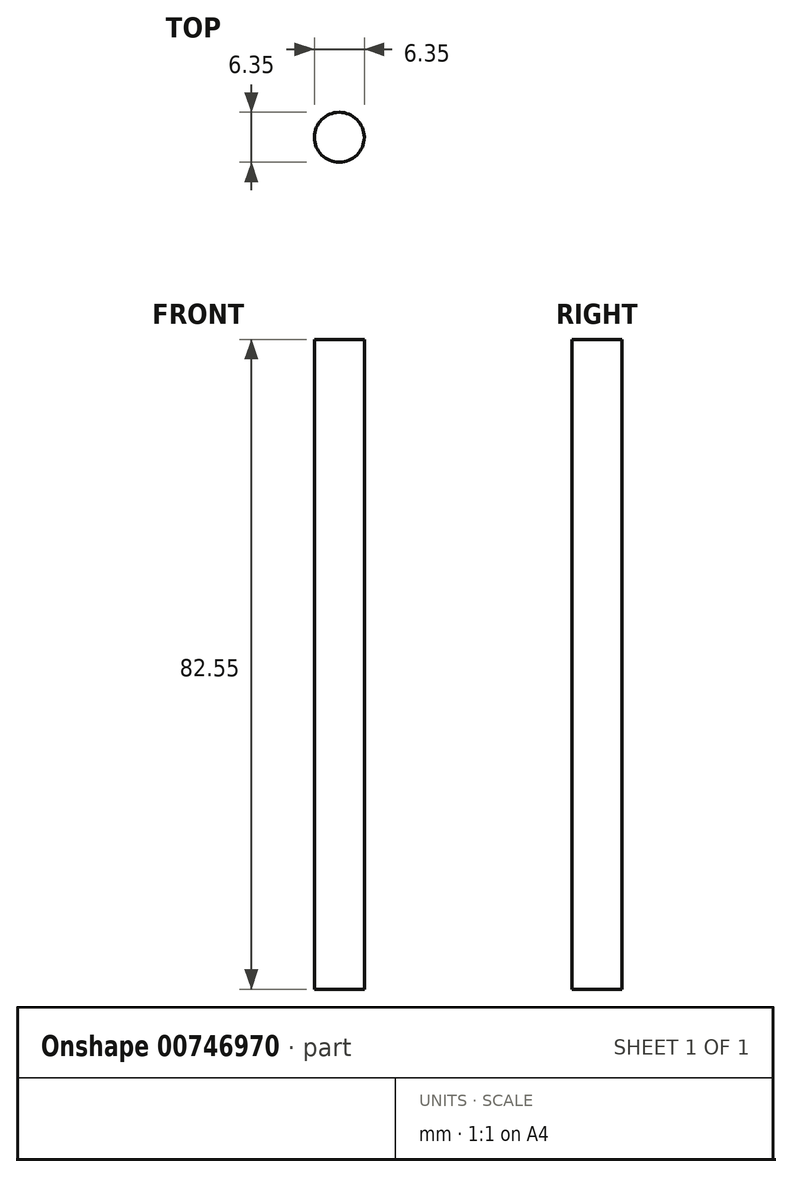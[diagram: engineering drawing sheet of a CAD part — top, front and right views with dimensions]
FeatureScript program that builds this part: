
annotation { "Feature Type Name" : "Feature", "Feature Type Description" : "" }
export const myFeature = defineFeature(function(context is Context, id is Id, definition is map)
    precondition{}
    {
        {
            var Q0;
            Q0=qCreatedBy(makeId("Top.planeOp"),FACE);
            var sketch = newSketch(context, id + "F0", { "sketchPlane" : qUnion([Q0])});
            skCircle(sketch, "E0", {"center": v(-1.7, -3.17) * mm, "radius": 3.18 * mm});
            skPoint(sketch, "E0.first.point", {"position": v(-1.72, 0) * mm});
            skPoint(sketch, "E0.second.point", {"position": v(0, -5.86) * mm});
            skPoint(sketch, "E0.third.point", {"position": v(-1.67, 0) * mm});
            skSolve(sketch);
        }
        {
            var Q0;
            Q0 = qSketchRegion(id + "F0", true);
            extrude(context, id + "F1", {"entities" : qUnion([Q0]), "depth" : 82.55 * mm, "offsetDistance" : 25.4 * mm});
        }
    });
